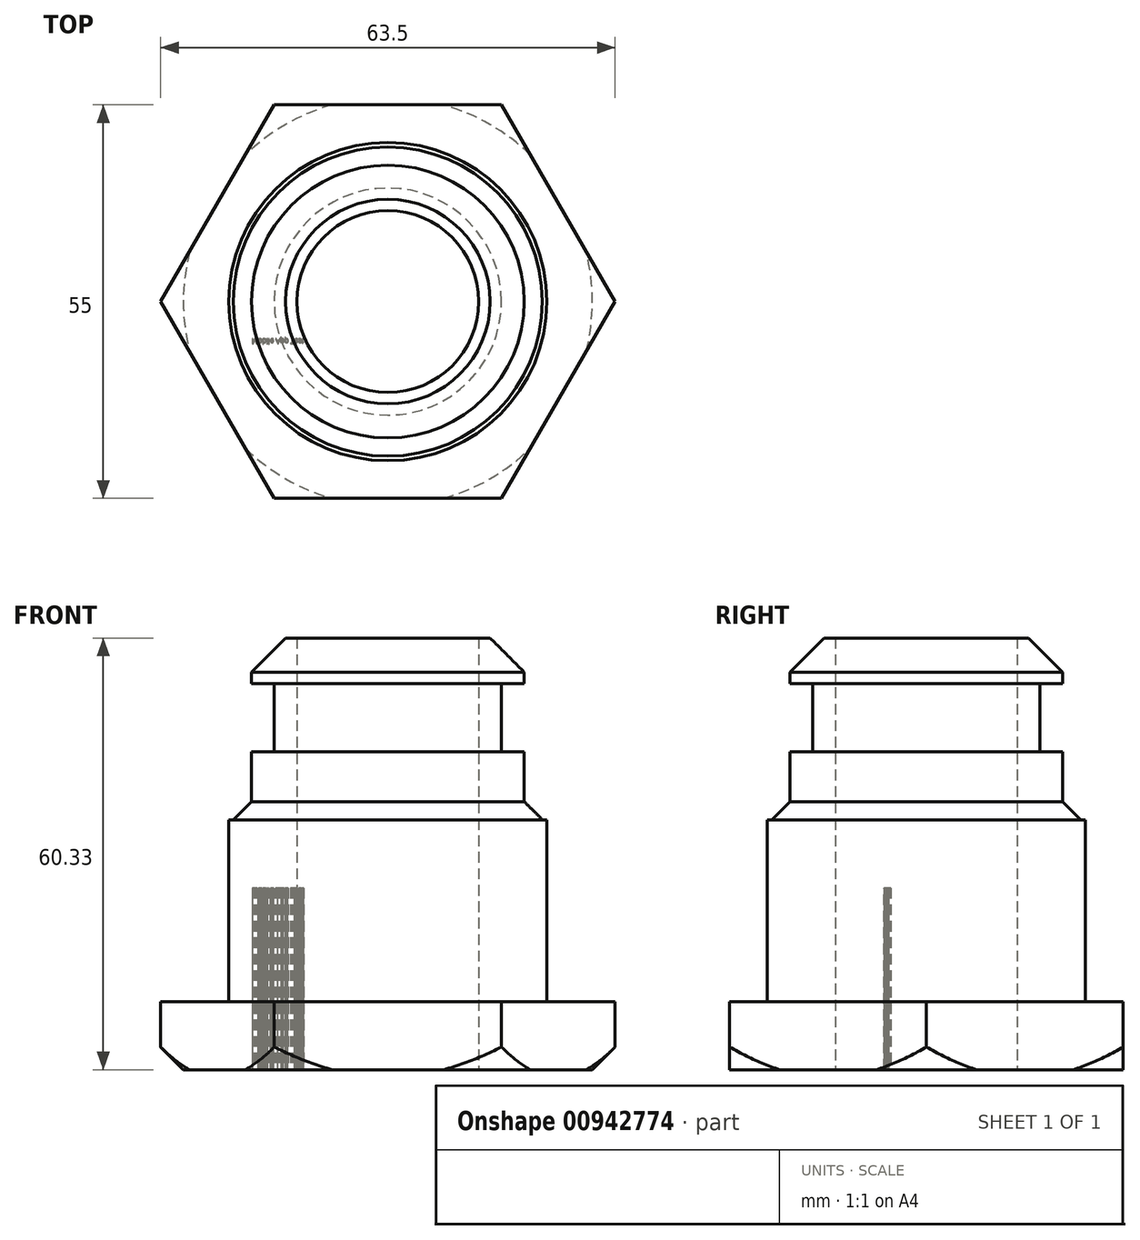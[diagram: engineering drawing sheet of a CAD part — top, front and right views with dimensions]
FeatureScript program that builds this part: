
annotation { "Feature Type Name" : "Feature", "Feature Type Description" : "" }
export const myFeature = defineFeature(function(context is Context, id is Id, definition is map)
    precondition{}
    {
        {
            var Q0;
            Q0=qCreatedBy(makeId("Front.planeOp"),FACE);
            var sketch = newSketch(context, id + "F0", { "sketchPlane" : qUnion([Q0])});
            skLineSegment(sketch, "E0", {"start": v(12.7, 0) * mm, "end": v(28.58, 0) * mm});
            skLineSegment(sketch, "E1", {"start": v(28.58, 0) * mm, "end": v(31.75, 3.18) * mm});
            skLineSegment(sketch, "E2", {"start": v(31.75, 3.18) * mm, "end": v(31.75, 9.53) * mm});
            skLineSegment(sketch, "E3", {"start": v(31.75, 9.53) * mm, "end": v(22.23, 9.53) * mm});
            skLineSegment(sketch, "E4", {"start": v(22.23, 9.53) * mm, "end": v(22.23, 34.92) * mm});
            skLineSegment(sketch, "E5", {"start": v(22.23, 34.93) * mm, "end": v(19.05, 34.93) * mm});
            skLineSegment(sketch, "E6", {"start": v(19.05, 34.93) * mm, "end": v(19.05, 44.45) * mm});
            skLineSegment(sketch, "E7", {"start": v(19.05, 44.45) * mm, "end": v(15.88, 44.45) * mm});
            skLineSegment(sketch, "E8", {"start": v(15.88, 44.45) * mm, "end": v(15.88, 53.98) * mm});
            skLineSegment(sketch, "E9", {"start": v(15.88, 53.98) * mm, "end": v(19.05, 53.98) * mm});
            skLineSegment(sketch, "E10", {"start": v(19.05, 53.98) * mm, "end": v(19.05, 60.33) * mm});
            skLineSegment(sketch, "E11", {"start": v(19.05, 60.33) * mm, "end": v(12.7, 60.33) * mm});
            skLineSegment(sketch, "E12", {"start": v(12.7, 60.33) * mm, "end": v(12.7, 0) * mm});
            skLineSegment(sketch, "E13", {"start": v(0, 0) * mm, "end": v(0, 60.33) * mm, "construction": true});
            skSolve(sketch);
        }
        {
            var Q0;
            Q0=makeQuery(id+"F0.imprint","IMPRINT",FACE,{"disambiguationData":[TD([[makeQuery(id+"F0.imprint","IMPRINT",EDGE,{"derivedFrom":sQuery(id+"F0.wireOp",EDGE,"E0")}),1.0]])]});
            var Q1;
            Q1=sQuery(id+"F0.wireOp",EDGE,"E13");
            revolve(context, id + "F1", {"surfaceOperationType" : NewSurfaceOperationType.NEW, "entities" : qUnion([Q0]), "axis" : qUnion([Q1]), "revolveType" : RevolveType.FULL});
        }
        {
            var Q0;
            Q0=makeQuery(id+"F1.opRevolve","SWEPT_EDGE",EDGE,{"disambiguationData":[OSD([sQuery(id+"F0.wireOp",EDGE,"E5"),sQuery(id+"F0.wireOp",EDGE,"E6")])]});
            chamfer(context, id + "F2", {"entities" : qUnion([Q0]), "width" : 2.54 * mm, "tangentPropagation" : true});
        }
        {
            var Q0;
            Q0=qCreatedBy(makeId("Top.planeOp"),FACE);
            var sketch = newSketch(context, id + "F3", { "sketchPlane" : qUnion([Q0])});
            skLineSegment(sketch, "E14.0", {"start": v(15.88, 27.5) * mm, "end": v(31.75, 0) * mm});
            skLineSegment(sketch, "E14.1", {"start": v(31.75, 0) * mm, "end": v(15.88, -27.5) * mm});
            skLineSegment(sketch, "E14.2", {"start": v(15.87, -27.5) * mm, "end": v(-15.88, -27.5) * mm});
            skLineSegment(sketch, "E14.3", {"start": v(-15.88, -27.5) * mm, "end": v(-31.75, 0) * mm});
            skLineSegment(sketch, "E14.4", {"start": v(-31.75, 0) * mm, "end": v(-15.87, 27.5) * mm});
            skLineSegment(sketch, "E14.5", {"start": v(-15.87, 27.5) * mm, "end": v(15.88, 27.5) * mm});
            skCircle(sketch, "E15", {"center": v(0, 0) * mm, "radius": 31.75 * mm});
            skSolve(sketch);
        }
        {
            var Q0;
            {var subQ0=sQuery(id+"F3.wireOp",EDGE,"E14.3");Q0=makeQuery(id+"F3.imprint","IMPRINT",FACE,{"disambiguationData":[TD([[makeQuery(id+"F3.imprint","IMPRINT",EDGE,{"derivedFrom":subQ0}),1.0]])]});}
            var Q1;
            {var subQ0=sQuery(id+"F3.wireOp",EDGE,"E14.4");Q1=makeQuery(id+"F3.imprint","IMPRINT",FACE,{"disambiguationData":[TD([[makeQuery(id+"F3.imprint","IMPRINT",EDGE,{"derivedFrom":subQ0}),1.0]])]});}
            var Q2;
            {var subQ0=sQuery(id+"F3.wireOp",EDGE,"E14.5");Q2=makeQuery(id+"F3.imprint","IMPRINT",FACE,{"disambiguationData":[TD([[makeQuery(id+"F3.imprint","IMPRINT",EDGE,{"derivedFrom":subQ0}),1.0]])]});}
            var Q3;
            {var subQ0=sQuery(id+"F3.wireOp",EDGE,"E14.0");Q3=makeQuery(id+"F3.imprint","IMPRINT",FACE,{"disambiguationData":[TD([[makeQuery(id+"F3.imprint","IMPRINT",EDGE,{"derivedFrom":subQ0}),1.0]])]});}
            var Q4;
            {var subQ0=sQuery(id+"F3.wireOp",EDGE,"E14.1");Q4=makeQuery(id+"F3.imprint","IMPRINT",FACE,{"disambiguationData":[TD([[makeQuery(id+"F3.imprint","IMPRINT",EDGE,{"derivedFrom":subQ0}),1.0]])]});}
            var Q5;
            {var subQ0=sQuery(id+"F3.wireOp",EDGE,"E14.2");Q5=makeQuery(id+"F3.imprint","IMPRINT",FACE,{"disambiguationData":[TD([[makeQuery(id+"F3.imprint","IMPRINT",EDGE,{"derivedFrom":subQ0}),1.0]])]});}
            extrude(context, id + "F4", {"entities" : qUnion([Q0, Q1, Q2, Q3, Q4, Q5]), "operationType" : NewBodyOperationType.REMOVE, "endBound" : BoundingType.THROUGH_ALL, "depth" : 25.4 * mm, "offsetDistance" : 25.4 * mm});
        }
        {
            var Q0;
            Q0=makeQuery(id+"F1.opRevolve","SWEPT_EDGE",EDGE,{"disambiguationData":[OSD([sQuery(id+"F0.wireOp",EDGE,"E10"),sQuery(id+"F0.wireOp",EDGE,"E11")])]});
            chamfer(context, id + "F5", {"entities" : qUnion([Q0]), "width" : 4.76 * mm, "tangentPropagation" : true});
        }
        {
            var Q0;
            Q0=makeQuery(id+"F1.opRevolve","SWEPT_FACE",FACE,{"disambiguationData":[OSD([sQuery(id+"F0.wireOp",EDGE,"E0")])]});
            var sketch = newSketch(context, id + "F6", { "sketchPlane" : qUnion([Q0])});
            skArc(sketch, "E16", {"start": v(-19.92, 0) * mm, "mid": v(2.77, 19.73) * mm, "end": v(19.15, -5.49) * mm, "construction": true});
            skText(sketch, "E17", { "text": "Mobile App Test", "fontName": "OpenSans-Regular.ttf"});
            const initialGuessF6  = {"E17": [-0.01902, 0.0052, 1, 0, 0.0007]};
            skSetInitialGuess(sketch, initialGuessF6);
            skSolve(sketch);
        }
        {
            var Q0;
            Q0 = qSketchRegion(id + "F6", true);
            extrude(context, id + "F7", {"entities" : qUnion([Q0]), "operationType" : NewBodyOperationType.REMOVE, "oppositeDirection" : true, "depth" : 25.4 * mm, "offsetDistance" : 25.4 * mm});
        }
    });
